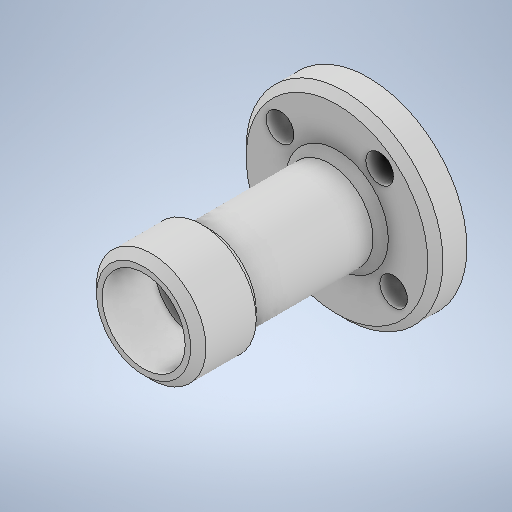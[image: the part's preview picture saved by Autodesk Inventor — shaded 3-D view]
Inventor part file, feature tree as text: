
AUTODESK INVENTOR PART (.ipt)
format: ipt  version: 2025.2 (Build 292293000, 293)  size: 497,152 bytes
history: native  units: in
note: dims shown in document units (in); Inventor stores cm internally (conversion verified against a paired STEP export)
features: sketch x5, extrude x4, chamfer x4, other x1
ambient origin geometry x8: Origin, YZ Plane, XZ Plane, XY Plane, X Axis, Y Axis, Z Axis, Center Point
bodies: Solid1 (feature_tree)
feature tree (14):
  extrude  "Extrusion1"  Depth=0.315in TaperAngle=0.0deg
  extrude  "Extrusion2"  Depth=1.2795in
  extrude  "Extrusion3"  TaperAngle=0.0deg  [1 undecoded]
  extrude  "Extrusion4"  Depth=1.1811in
  chamfer  "Chamfer1"  Distance=2.5354in
  chamfer  "Chamfer2"  Distance=1.4961in
  chamfer  "Chamfer3"  Distance=0.9449in
  chamfer  "Chamfer4"  Distance=0.1378in Angle=45.0deg
  sketch  "Sketch1"  dims[d3=3.5433in d4=0.315in d5=0.0in]
  other  "Image1"
  sketch  "Sketch2"  dims[d9=1.5748in d11=360.0deg d13=0.0in d14=0.0in]
  sketch  "Sketch Circular Pattern1"  dims[d7=0.5in d8=1.2795in]
  sketch  "Sketch3"  dims[d16=1.5748in d17=1.1811in d18=2.5354in d19=0.0in]
  sketch  "Sketch4"  dims[d20=1.9685in d21=1.4961in d22=0.9449in d23=0.2362in d24=0.0in d25=0.0in d26=0.1378in d27=0.0787in d28=45.0deg d29=0.1378in d30=0.0787in d31=45.0deg d32=0.1378in d33=0.0787in d34=45.0deg d35=0.252in d36=0.0in d37=0.1378in d38=0.0787in d39=45.0deg]
note: 1 required parameter value undecoded (feature->parameter linkage not recoverable at this tier; creation-order binding heuristic only, values carry confidence <= 0.55)
